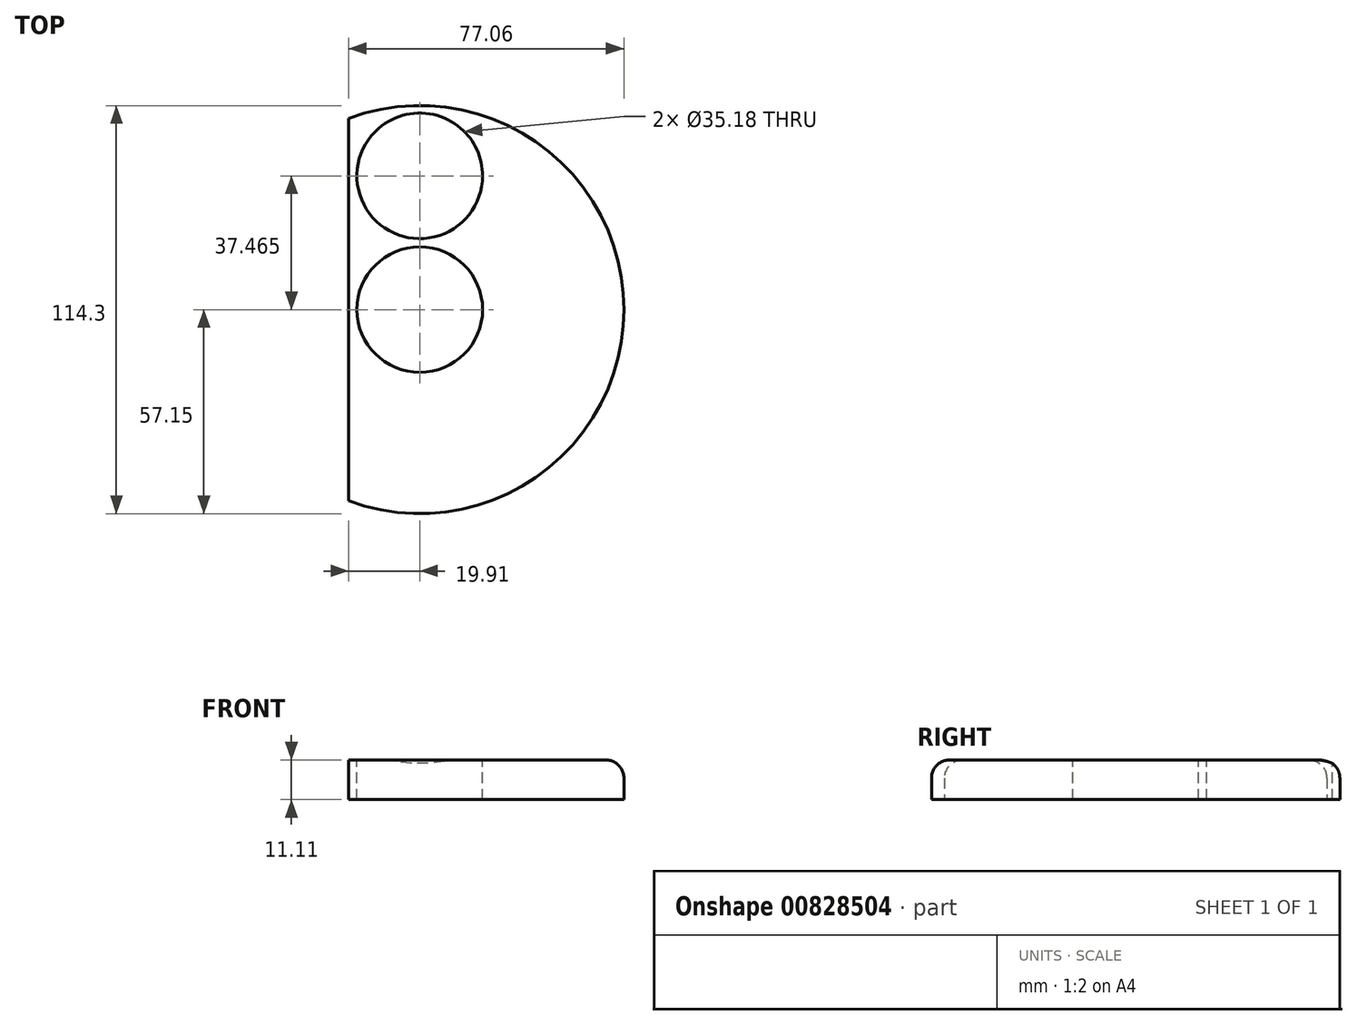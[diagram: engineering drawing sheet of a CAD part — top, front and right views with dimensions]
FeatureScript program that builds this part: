
annotation { "Feature Type Name" : "Feature", "Feature Type Description" : "" }
export const myFeature = defineFeature(function(context is Context, id is Id, definition is map)
    precondition{}
    {
        {
            var Q0;
            Q0=qCreatedBy(makeId("Top.planeOp"),FACE);
            var sketch = newSketch(context, id + "F0", { "sketchPlane" : qUnion([Q0])});
            skCircle(sketch, "E0", {"center": v(0, 0) * mm, "radius": 57.15 * mm});
            skSolve(sketch);
        }
        {
            var Q0;
            Q0 = qSketchRegion(id + "F0", true);
            extrude(context, id + "F1", {"entities" : qUnion([Q0]), "depth" : 11.1 * mm, "offsetDistance" : 25.4 * mm});
        }
        {
            var Q0;
            Q0=makeQuery(id+"F1.opExtrude","CAP_FACE",FACE,{"disambiguationData":[OSD([sQuery(id+"F0.wireOp",EDGE,"E0")])],"isStart":false});
            var sketch = newSketch(context, id + "F2", { "sketchPlane" : qUnion([Q0])});
            skCircle(sketch, "E1", {"center": v(0, 0) * mm, "radius": 17.59 * mm});
            skSolve(sketch);
        }
        {
            var Q0;
            Q0 = qSketchRegion(id + "F2", true);
            extrude(context, id + "F3", {"entities" : qUnion([Q0]), "operationType" : NewBodyOperationType.REMOVE, "oppositeDirection" : true, "depth" : 25.4 * mm, "offsetDistance" : 25.4 * mm});
        }
        {
            var Q0;
            Q0=makeQuery(id+"F1.opExtrude","CAP_FACE",FACE,{"disambiguationData":[OSD([sQuery(id+"F0.wireOp",EDGE,"E0")])],"isStart":false});
            var sketch = newSketch(context, id + "F4", { "sketchPlane" : qUnion([Q0])});
            skCircle(sketch, "E2", {"center": v(0, 37.47) * mm, "radius": 17.59 * mm});
            skSolve(sketch);
        }
        {
            var Q0;
            Q0 = qSketchRegion(id + "F4", true);
            extrude(context, id + "F5", {"entities" : qUnion([Q0]), "operationType" : NewBodyOperationType.REMOVE, "endBound" : BoundingType.THROUGH_ALL, "oppositeDirection" : true, "depth" : 25.4 * mm, "offsetDistance" : 25.4 * mm});
        }
        {
            var Q0;
            Q0=qCreatedBy(makeId("Front.planeOp"),FACE);
            var sketch = newSketch(context, id + "F6", { "sketchPlane" : qUnion([Q0])});
            skLineSegment(sketch, "E3", {"start": v(0, -48.4) * mm, "end": v(0, 89.43) * mm});
            skSolve(sketch);
        }
        {
            var Q0;
            Q0=makeQuery(id+"F1.opExtrude","CAP_FACE",FACE,{"disambiguationData":[OSD([sQuery(id+"F0.wireOp",EDGE,"E0")])],"isStart":false});
            var sketch = newSketch(context, id + "F7", { "sketchPlane" : qUnion([Q0])});
            skArc(sketch, "E4", {"start": v(-29.19, 24.3) * mm, "mid": v(-20.43, 36.95) * mm, "end": v(-23.8, 51.96) * mm});
            skArc(sketch, "E5", {"start": v(-29.19, 24.3) * mm, "mid": v(-35.93, 17.53) * mm, "end": v(-33.04, 8.42) * mm});
            skArc(sketch, "E6", {"start": v(-33.04, 8.42) * mm, "mid": v(-47.74, 7.34) * mm, "end": v(-57, -4.13) * mm});
            skArc(sketch, "E7", {"start": v(-23.8, 51.96) * mm, "mid": v(-54.97, 32.53) * mm, "end": v(-57, -4.13) * mm});
            skSolve(sketch);
        }
        {
            var Q0;
            Q0 = qSketchRegion(id + "F7", true);
            extrude(context, id + "F8", {"entities" : qUnion([Q0]), "operationType" : NewBodyOperationType.REMOVE, "endBound" : BoundingType.THROUGH_ALL, "oppositeDirection" : true, "depth" : 25.4 * mm, "offsetDistance" : 25.4 * mm});
        }
        {
            var Q0;
            Q0=qCreatedBy(makeId("Front.planeOp"),FACE);
            var sketch = newSketch(context, id + "F9", { "sketchPlane" : qUnion([Q0])});
            skLineSegment(sketch, "E8", {"start": v(0, 0) * mm, "end": v(0, -103.47) * mm});
            skSolve(sketch);
        }
        {
            var Q0;
            {var subQ0=sQuery(id+"F0.wireOp",EDGE,"E0");var subQ3=makeQuery(id+"F8.boolean.opBoolean","COPY",FACE,{"derivedFrom":makeQuery(id+"F8.opExtrude","SWEPT_FACE",FACE,{"disambiguationData":[OSD([sQuery(id+"F7.wireOp",EDGE,"E6")])]})});Q0=makeQuery(id+"Fy26xBKjoRHN8u7_1.2.F8.boolean.opBoolean","SPLIT",EDGE,{"disambiguationData":[TD([subQ3])],"derivedFrom":makeQuery(id+"Fy26xBKjoRHN8u7_1.1.F8.boolean.opBoolean","SPLIT",EDGE,{"disambiguationData":[TD([subQ3])],"derivedFrom":makeQuery(id+"F1.opExtrude","CAP_EDGE",EDGE,{"disambiguationData":[OSD([subQ0])],"isStart":false})})});}
            var Q1;
            {var subQ0=sQuery(id+"F0.wireOp",EDGE,"E0");var subQ2=makeQuery(id+"Fy26xBKjoRHN8u7_1.1.F8.opExtrude","SWEPT_FACE",FACE,{"disambiguationData":[OSD([sQuery(id+"F7.wireOp",EDGE,"E4")])]});var subQ3=sQuery(id+"F7.wireOp",EDGE,"E6");Q1=makeQuery(id+"Fy26xBKjoRHN8u7_1.2.F8.boolean.opBoolean","SPLIT",EDGE,{"disambiguationData":[TD([makeQuery(id+"Fy26xBKjoRHN8u7_1.1.F8.boolean.opBoolean","COPY",FACE,{"derivedFrom":subQ2})])],"derivedFrom":makeQuery(id+"Fy26xBKjoRHN8u7_1.1.F8.boolean.opBoolean","SPLIT",EDGE,{"disambiguationData":[TD([makeQuery(id+"F8.boolean.opBoolean","COPY",FACE,{"derivedFrom":makeQuery(id+"F8.opExtrude","SWEPT_FACE",FACE,{"disambiguationData":[OSD([subQ3])]})})])],"derivedFrom":makeQuery(id+"F1.opExtrude","CAP_EDGE",EDGE,{"disambiguationData":[OSD([subQ0])],"isStart":false})})});}
            var Q2;
            {var subQ0=sQuery(id+"F0.wireOp",EDGE,"E0");Q2=makeQuery(id+"Fy26xBKjoRHN8u7_1.1.F8.boolean.opBoolean","SPLIT",EDGE,{"disambiguationData":[TD([makeQuery(id+"F8.boolean.opBoolean","COPY",FACE,{"derivedFrom":makeQuery(id+"F8.opExtrude","SWEPT_FACE",FACE,{"disambiguationData":[OSD([sQuery(id+"F7.wireOp",EDGE,"E4")])]})})])],"derivedFrom":makeQuery(id+"F1.opExtrude","CAP_EDGE",EDGE,{"disambiguationData":[OSD([subQ0])],"isStart":false})});}
            fillet(context, id + "F10", {"entities" : qUnion([Q0, Q1, Q2]), "radius" : 5.08 * mm, "tangentPropagation" : true, "allowEdgeOverflow" : false});
        }
        {
            var Q0;
            Q0=makeQuery(id+"F1.opExtrude","CAP_FACE",FACE,{"disambiguationData":[OSD([sQuery(id+"F0.wireOp",EDGE,"E0")])],"isStart":false});
            var sketch = newSketch(context, id + "F11", { "sketchPlane" : qUnion([Q0])});
            skLineSegment(sketch, "E9.bottom", {"start": v(-19.9, 61.6) * mm, "end": v(-59.22, 61.6) * mm});
            skLineSegment(sketch, "E9.top", {"start": v(-19.9, -63.86) * mm, "end": v(-59.22, -63.86) * mm});
            skLineSegment(sketch, "E9.left", {"start": v(-19.9, 61.6) * mm, "end": v(-19.9, -63.86) * mm});
            skLineSegment(sketch, "E9.right", {"start": v(-59.22, 61.6) * mm, "end": v(-59.22, -63.86) * mm});
            skSolve(sketch);
        }
        {
            var Q0;
            Q0 = qSketchRegion(id + "F11", true);
            extrude(context, id + "F12", {"entities" : qUnion([Q0]), "operationType" : NewBodyOperationType.REMOVE, "endBound" : BoundingType.THROUGH_ALL, "oppositeDirection" : true, "depth" : 25.4 * mm, "offsetDistance" : 25.4 * mm});
        }
    });
